# Revit family: 797270001_Llave Jardín Liviana Satinada
name_source: partatom
category: Plumbing Fixtures
units: mm (PartAtom-declared; Revit-internal decimal feet)

## family parameters
Always vertical = Yes
Cut with Voids When Loaded = No
Host = Wall
OmniClass Number = 23.27.43.00
OmniClass Title = Pipe Fittings
Part Type = Normal
Room Calculation Point = No
Round Connector Dimension = Use Diameter
Shared = No

## types (1)
- Type 1
    Acabados = Satinado
    Alto = 79 mm
    Altura LLave = 1000 mm  [stored 3.28084 ft]
    Ancho = 52 mm
    Capacidad de flujo estimada real a 20 psi = 31,86 L/min
    Ciclo de vida de la unidad de cierre = 500.000 ciclos
    Creado por = IDD
    Description = La grifería llave jrd corr 1/2P salida 3/4P cr- sat ha sido diseñada para trabajar en perfecta armonía con el espacio; inspirada en las necesidades del consumidor latinoamericano dando como resultado un producto robusto y funcional.
•
Manija con sistema de cierre a compresión.
•
Para trabajo pesado, alto caudal.
•
Con acabado robusto y resistente.
    Fabricante = Grival
    Fecha de creación = 10/08/2020
    Garantía = 5 Años
    Longitud = 102 mm
    Material = Latón
    Peso Bruto aprox = 200 gr. - 0,44 lb.
    Peso Neto aprox = 178 gr. - 0,39 lb
    Presión máxima recomendada = 125 psi
    Presión mínima recomendada = 20 psi.
    Referencia = 797270001
    Temperaturas máxima de trabajo = 71 ºC / 159,8 ºF
    Temperaturas mínima de trabajo = 5 ºC / 41 ºF
    URL = https://www.grival.com

note: [stored X ft] marks values corroborated as IEEE doubles in the binary element streams (Revit-internal decimal feet)

## geometry (parser evidence)
native form markers: Sweep x8
no freeform markers — native parametric forms only
